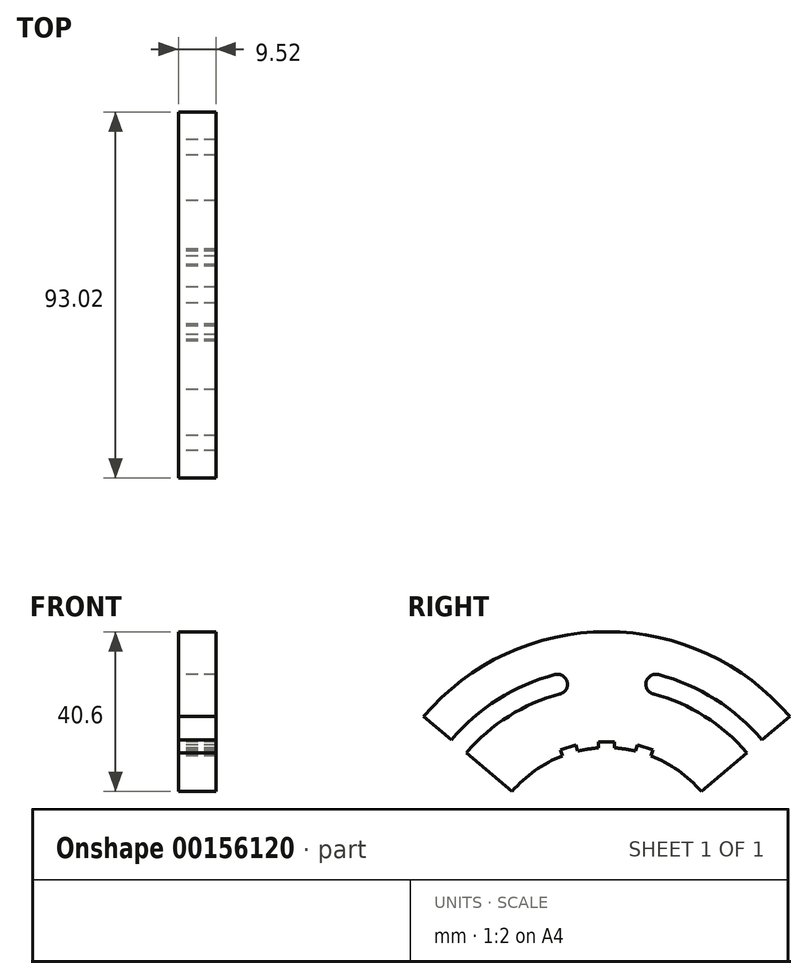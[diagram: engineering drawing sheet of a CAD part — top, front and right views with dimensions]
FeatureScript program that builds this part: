
annotation { "Feature Type Name" : "Feature", "Feature Type Description" : "" }
export const myFeature = defineFeature(function(context is Context, id is Id, definition is map)
    precondition{}
    {
        {
            var Q0;
            Q0=qCreatedBy(makeId("Right.planeOp"),FACE);
            var sketch = newSketch(context, id + "F0", { "sketchPlane" : qUnion([Q0])});
            skArc(sketch, "E0", {"start": v(24.03, 4.14) * mm, "mid": v(18.2, 9.47) * mm, "end": v(11.24, 13.2) * mm});
            skArc(sketch, "E1", {"start": v(32.07, 21.12) * mm, "mid": v(0.49, 33) * mm, "end": v(-31.32, 21.75) * mm, "construction": true});
            skLineSegment(sketch, "E2.bottom", {"start": v(-2.03, 16.8) * mm, "end": v(2.03, 16.8) * mm, "construction": true});
            skLineSegment(sketch, "E2.top", {"start": v(-2.03, 15.27) * mm, "end": v(-1.94, 15.27) * mm, "construction": true});
            skLineSegment(sketch, "E2.left", {"start": v(-2.03, 16.8) * mm, "end": v(-2.03, 15.27) * mm, "construction": true});
            skLineSegment(sketch, "E2.right", {"start": v(2.03, 16.8) * mm, "end": v(2.03, 15.27) * mm, "construction": true});
            skPoint(sketch, "E2.middle", {"position": v(0, 16.03) * mm});
            skArc(sketch, "E3.MirrorC", {"start": v(11.85, 28.93) * mm, "mid": v(10.03, 32.03) * mm, "end": v(13.13, 33.84) * mm});
            skArc(sketch, "E4.0", {"start": v(35.61, 13.96) * mm, "mid": v(24.88, 23.27) * mm, "end": v(11.85, 28.93) * mm});
            skArc(sketch, "E5.0", {"start": v(39.49, 17.24) * mm, "mid": v(27.59, 27.57) * mm, "end": v(13.13, 33.84) * mm});
            skArc(sketch, "E6", {"start": v(-13.13, 33.84) * mm, "mid": v(-10.03, 32.03) * mm, "end": v(-11.85, 28.93) * mm});
            skArc(sketch, "E7.MirrorCS", {"start": v(-35.61, 13.96) * mm, "mid": v(-24.88, 23.27) * mm, "end": v(-11.85, 28.93) * mm});
            skArc(sketch, "E8.MirrorCS", {"start": v(-39.49, 17.24) * mm, "mid": v(-27.59, 27.57) * mm, "end": v(-13.13, 33.84) * mm});
            skArc(sketch, "E9", {"start": v(46.5, 23.2) * mm, "mid": v(0, 44.74) * mm, "end": v(-46.5, 23.2) * mm});
            skPoint(sketch, "E10.orphan", {"position": v(58.4, 21.55) * mm});
            skPoint(sketch, "E11.start.orphan", {"position": v(-58.4, 21.55) * mm});
            skLineSegment(sketch, "E12", {"start": v(24.03, 4.14) * mm, "end": v(35.61, 13.96) * mm});
            skLineSegment(sketch, "E13.MirrorCS", {"start": v(-24.03, 4.14) * mm, "end": v(-35.61, 13.96) * mm});
            skPoint(sketch, "E14.trimOffspring.end.orphan", {"position": v(50.68, 17.67) * mm});
            skPoint(sketch, "E15.orphan", {"position": v(43.03, 12.55) * mm});
            skPoint(sketch, "E16.end.orphan", {"position": v(38.8, 9.73) * mm});
            skPoint(sketch, "E17.orphan", {"position": v(27, 0) * mm});
            skPoint(sketch, "E18.trimOffspring.end.orphan", {"position": v(-50.68, 17.67) * mm});
            skLineSegment(sketch, "E19.trimOffspring", {"start": v(-39.49, 17.24) * mm, "end": v(-46.5, 23.2) * mm});
            skPoint(sketch, "E20.orphan", {"position": v(-43.03, 12.55) * mm});
            skPoint(sketch, "E21.MirrorCS.end.orphan", {"position": v(-38.8, 9.73) * mm});
            skPoint(sketch, "E21.MirrorCS.start.orphan", {"position": v(-27, 0) * mm});
            skLineSegment(sketch, "E22.trimOffspring", {"start": v(39.49, 17.24) * mm, "end": v(46.5, 23.2) * mm});
            skLineSegment(sketch, "E23.1.0", {"start": v(7.83, 15.92) * mm, "end": v(11.71, 14.71) * mm, "construction": true});
            skLineSegment(sketch, "E23.1.1", {"start": v(7.83, 15.92) * mm, "end": v(7.38, 14.46) * mm, "construction": true});
            skLineSegment(sketch, "E23.1.2", {"start": v(11.71, 14.71) * mm, "end": v(11.26, 13.26) * mm, "construction": true});
            skLineSegment(sketch, "E23.1.3", {"start": v(7.38, 14.46) * mm, "end": v(7.47, 14.43) * mm, "construction": true});
            skLineSegment(sketch, "E23.anchor1", {"start": v(0, -16.23) * mm, "end": v(-2.03, 16.8) * mm, "construction": true});
            skLineSegment(sketch, "E23.anchor2", {"start": v(0, -16.23) * mm, "end": v(7.47, 14.43) * mm, "construction": true});
            skLineSegment(sketch, "E24.MirrorCS", {"start": v(-7.83, 15.92) * mm, "end": v(-7.38, 14.46) * mm, "construction": true});
            skLineSegment(sketch, "E25.MirrorCS", {"start": v(-7.83, 15.92) * mm, "end": v(-11.71, 14.71) * mm, "construction": true});
            skLineSegment(sketch, "E26.MirrorCS", {"start": v(-11.71, 14.71) * mm, "end": v(-11.26, 13.26) * mm, "construction": true});
            skLineSegment(sketch, "E27", {"start": v(0, 44.74) * mm, "end": v(0, -16.23) * mm, "construction": true});
            skLineSegment(sketch, "E28", {"start": v(11.71, 14.71) * mm, "end": v(11.24, 13.2) * mm});
            skLineSegment(sketch, "E29", {"start": v(11.71, 14.71) * mm, "end": v(7.83, 15.92) * mm});
            skLineSegment(sketch, "E30", {"start": v(7.83, 15.92) * mm, "end": v(7, 13.22) * mm});
            skArc(sketch, "E31.trimOffspring", {"start": v(7.45, 14.37) * mm, "mid": v(4.76, 14.9) * mm, "end": v(2.03, 15.2) * mm});
            skLineSegment(sketch, "E32", {"start": v(2.03, 16.8) * mm, "end": v(2.03, 15.2) * mm});
            skLineSegment(sketch, "E33", {"start": v(2.03, 16.8) * mm, "end": v(-2.03, 16.8) * mm});
            skLineSegment(sketch, "E34", {"start": v(-2.03, 16.8) * mm, "end": v(-2.03, 15.2) * mm});
            skLineSegment(sketch, "E35", {"start": v(-7.83, 15.92) * mm, "end": v(-11.71, 14.71) * mm});
            skLineSegment(sketch, "E36", {"start": v(-7.83, 15.92) * mm, "end": v(-7.36, 14.4) * mm});
            skLineSegment(sketch, "E37", {"start": v(-11.71, 14.71) * mm, "end": v(-11.24, 13.2) * mm});
            skArc(sketch, "E38.trimOffspring", {"start": v(-1.93, 15.2) * mm, "mid": v(-4.66, 14.92) * mm, "end": v(-7.36, 14.4) * mm});
            skArc(sketch, "E39.trimOffspring", {"start": v(-11.24, 13.2) * mm, "mid": v(-18.2, 9.47) * mm, "end": v(-24.03, 4.14) * mm});
            skPoint(sketch, "E40.orphan", {"position": v(-7.38, 14.46) * mm});
            skPoint(sketch, "E41.MirrorCS.end.orphan", {"position": v(-11.26, 13.26) * mm});
            skSolve(sketch);
        }
        {
            var Q0;
            Q0 = qSketchRegion(id + "F0", true);
            extrude(context, id + "F1", {"entities" : qUnion([Q0]), "depth" : 3.17 * mm});
        }
        {
            var Q0;
            Q0=makeQuery(id+"F1.opExtrude","CAP_FACE",FACE,{"disambiguationData":[OSD([sQuery(id+"F0.wireOp",EDGE,"E0"),sQuery(id+"F0.wireOp",EDGE,"E3.MirrorC"),sQuery(id+"F0.wireOp",EDGE,"E4.0"),sQuery(id+"F0.wireOp",EDGE,"E5.0"),sQuery(id+"F0.wireOp",EDGE,"E6"),sQuery(id+"F0.wireOp",EDGE,"E7.MirrorCS"),sQuery(id+"F0.wireOp",EDGE,"E8.MirrorCS"),sQuery(id+"F0.wireOp",EDGE,"E9"),sQuery(id+"F0.wireOp",EDGE,"E12"),sQuery(id+"F0.wireOp",EDGE,"E13.MirrorCS"),sQuery(id+"F0.wireOp",EDGE,"E19.trimOffspring"),sQuery(id+"F0.wireOp",EDGE,"E22.trimOffspring")])],"isStart":true});
            var sketch = newSketch(context, id + "F2", { "sketchPlane" : qUnion([Q0])});
            skLineSegment(sketch, "E42.0", {"start": v(-24.03, 4.14) * mm, "end": v(-24.03, 4.14) * mm});
            skLineSegment(sketch, "E43.bottom", {"start": v(2.03, 16.8) * mm, "end": v(-2.03, 16.8) * mm});
            skLineSegment(sketch, "E43.top", {"start": v(2.03, 15.27) * mm, "end": v(-2.03, 15.27) * mm});
            skLineSegment(sketch, "E43.left", {"start": v(2.03, 16.8) * mm, "end": v(2.03, 15.27) * mm});
            skLineSegment(sketch, "E43.right", {"start": v(-2.03, 16.8) * mm, "end": v(-2.03, 15.27) * mm});
            skPoint(sketch, "E43.middle", {"position": v(0, 16.03) * mm});
            skLineSegment(sketch, "E44.1.0", {"start": v(11.71, 14.71) * mm, "end": v(7.83, 15.92) * mm});
            skLineSegment(sketch, "E44.1.1", {"start": v(11.71, 14.71) * mm, "end": v(11.26, 13.26) * mm});
            skLineSegment(sketch, "E44.1.2", {"start": v(11.26, 13.26) * mm, "end": v(7.38, 14.46) * mm});
            skLineSegment(sketch, "E44.1.3", {"start": v(7.83, 15.92) * mm, "end": v(7.38, 14.46) * mm});
            skLineSegment(sketch, "E44.anchor1", {"start": v(0, -16.23) * mm, "end": v(-2.03, 16.8) * mm, "construction": true});
            skLineSegment(sketch, "E44.anchor2", {"start": v(0, -16.23) * mm, "end": v(7.83, 15.92) * mm, "construction": true});
            skLineSegment(sketch, "E45.1.0", {"start": v(2.93, -49.19) * mm, "end": v(6.95, -48.58) * mm});
            skLineSegment(sketch, "E45.1.1", {"start": v(2.93, -49.19) * mm, "end": v(2.7, -47.68) * mm});
            skLineSegment(sketch, "E45.1.2", {"start": v(2.7, -47.68) * mm, "end": v(6.72, -47.07) * mm});
            skLineSegment(sketch, "E45.1.3", {"start": v(6.95, -48.58) * mm, "end": v(6.72, -47.07) * mm});
            skLineSegment(sketch, "E45.2.0", {"start": v(-7.83, 15.92) * mm, "end": v(-11.71, 14.71) * mm});
            skLineSegment(sketch, "E45.2.1", {"start": v(-7.83, 15.92) * mm, "end": v(-7.38, 14.46) * mm});
            skLineSegment(sketch, "E45.2.2", {"start": v(-7.38, 14.46) * mm, "end": v(-11.26, 13.26) * mm});
            skLineSegment(sketch, "E45.2.3", {"start": v(-11.71, 14.71) * mm, "end": v(-11.26, 13.26) * mm});
            skLineSegment(sketch, "E45.anchor2", {"start": v(0, -16.23) * mm, "end": v(-11.71, 14.71) * mm, "construction": true});
            skSolve(sketch);
        }
        {
            var Q0;
            Q0=makeQuery(id+"F2.imprint","IMPRINT",FACE,{"disambiguationData":[TD([[makeQuery(id+"F2.imprint","IMPRINT",EDGE,{"derivedFrom":sQuery(id+"F2.wireOp",EDGE,"E45.2.0")}),1.0]])]});
            var Q1;
            Q1=makeQuery(id+"F2.imprint","IMPRINT",FACE,{"disambiguationData":[TD([[makeQuery(id+"F2.imprint","IMPRINT",EDGE,{"derivedFrom":sQuery(id+"F2.wireOp",EDGE,"E43.bottom")}),1.0]])]});
            var Q2;
            Q2=makeQuery(id+"F2.imprint","IMPRINT",FACE,{"disambiguationData":[TD([[makeQuery(id+"F2.imprint","IMPRINT",EDGE,{"derivedFrom":sQuery(id+"F2.wireOp",EDGE,"E44.1.0")}),1.0]])]});
            extrude(context, id + "F3", {"entities" : qUnion([Q0, Q1, Q2]), "operationType" : NewBodyOperationType.ADD, "depth" : 6.35 * mm});
        }
    });
